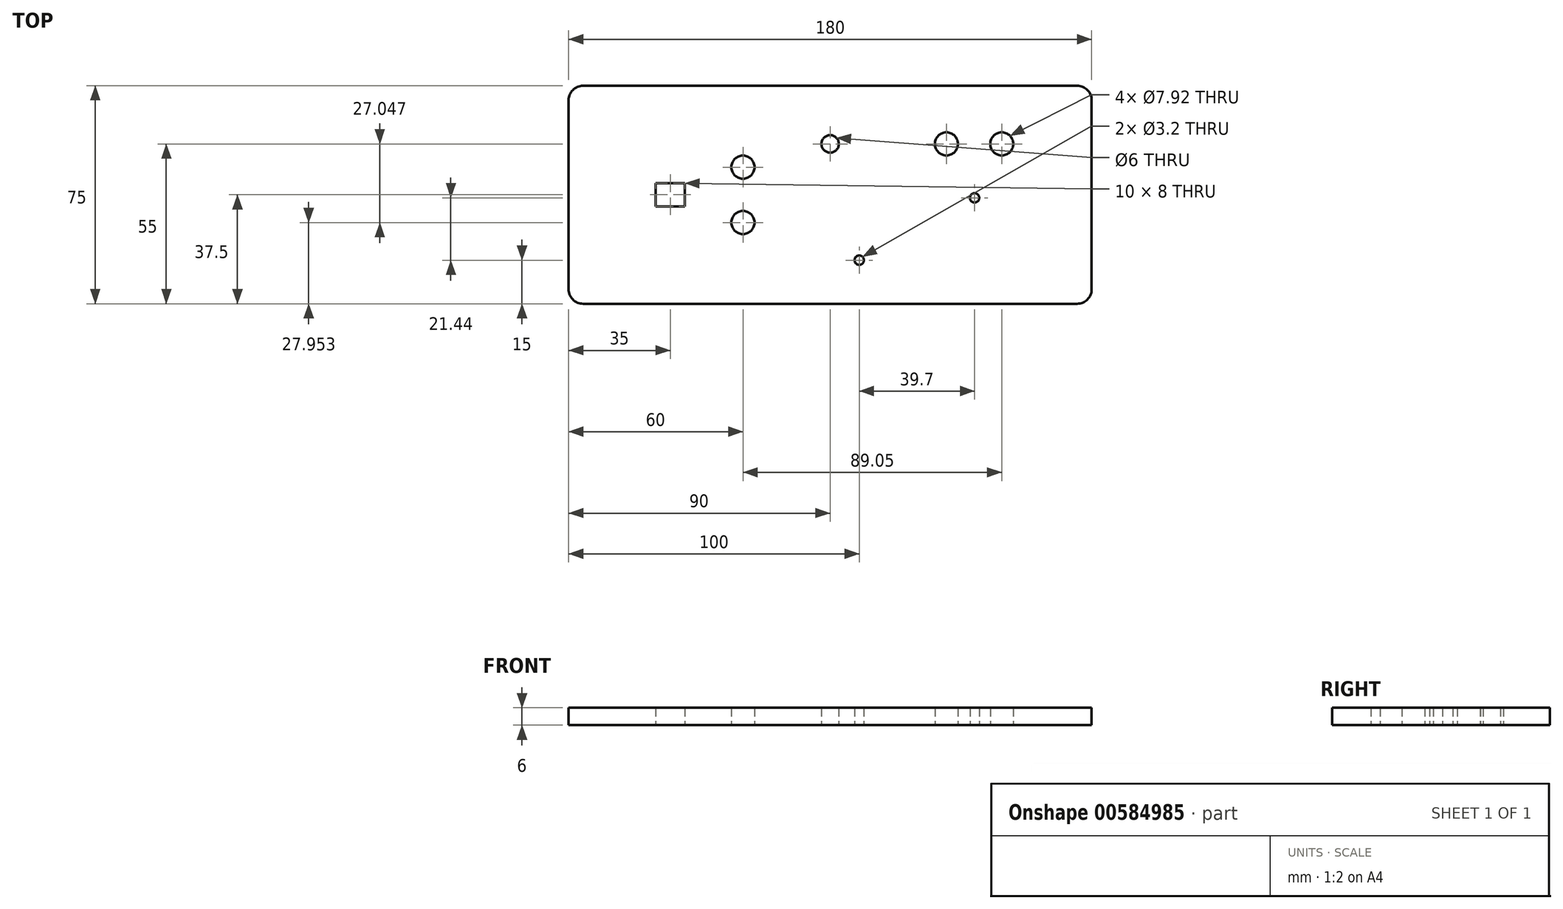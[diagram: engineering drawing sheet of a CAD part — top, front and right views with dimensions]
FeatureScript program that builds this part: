
annotation { "Feature Type Name" : "Feature", "Feature Type Description" : "" }
export const myFeature = defineFeature(function(context is Context, id is Id, definition is map)
    precondition{}
    {
        {
            var Q0;
            Q0=qCreatedBy(makeId("Top.planeOp"),FACE);
            var sketch = newSketch(context, id + "F0", { "sketchPlane" : qUnion([Q0])});
            skLineSegment(sketch, "E0.bottom", {"start": v(-90, 37.5) * mm, "end": v(90, 37.5) * mm});
            skLineSegment(sketch, "E0.top", {"start": v(-90, -37.5) * mm, "end": v(90, -37.5) * mm});
            skLineSegment(sketch, "E0.left", {"start": v(-90, 37.5) * mm, "end": v(-90, -37.5) * mm});
            skLineSegment(sketch, "E0.right", {"start": v(90, 37.5) * mm, "end": v(90, -37.5) * mm});
            skPoint(sketch, "E0.middle", {"position": v(0, 0) * mm});
            skLineSegment(sketch, "E1.bottom", {"start": v(-50, -4) * mm, "end": v(-60, -4) * mm});
            skLineSegment(sketch, "E1.top", {"start": v(-50, 4) * mm, "end": v(-60, 4) * mm});
            skLineSegment(sketch, "E1.left", {"start": v(-50, -4) * mm, "end": v(-50, 4) * mm});
            skLineSegment(sketch, "E1.right", {"start": v(-60, -4) * mm, "end": v(-60, 4) * mm});
            skPoint(sketch, "E1.middle", {"position": v(-55, 0) * mm});
            skCircle(sketch, "E2", {"center": v(-30, 9.5) * mm, "radius": 3.96 * mm});
            skCircle(sketch, "E3", {"center": v(-30, -9.55) * mm, "radius": 3.96 * mm});
            skCircle(sketch, "E4", {"center": v(10, -22.5) * mm, "radius": 1.6 * mm});
            skCircle(sketch, "E5", {"center": v(49.7, -1.06) * mm, "radius": 1.6 * mm});
            skCircle(sketch, "E6", {"center": v(0, 17.5) * mm, "radius": 3 * mm});
            skCircle(sketch, "E7", {"center": v(40, 17.5) * mm, "radius": 3.96 * mm});
            skCircle(sketch, "E8", {"center": v(59.05, 17.5) * mm, "radius": 3.96 * mm});
            skLineSegment(sketch, "E9", {"start": v(-30, 9.5) * mm, "end": v(-30, -9.55) * mm});
            skSolve(sketch);
        }
        {
            var Q0;
            Q0=makeQuery(id+"F0.imprint","IMPRINT",FACE,{"disambiguationData":[TD([[makeQuery(id+"F0.imprint","IMPRINT",EDGE,{"derivedFrom":sQuery(id+"F0.wireOp",EDGE,"E0.bottom")}),-1.0]])]});
            extrude(context, id + "F1", {"entities" : qUnion([Q0]), "depth" : 6 * mm, "offsetDistance" : 25 * mm});
        }
        {
            var Q0;
            Q0=makeQuery(id+"F1.opExtrude","SWEPT_EDGE",EDGE,{"disambiguationData":[OSD([sQuery(id+"F0.wireOp",EDGE,"E0.bottom"),sQuery(id+"F0.wireOp",EDGE,"E0.left")])]});
            var Q1;
            Q1=makeQuery(id+"F1.opExtrude","SWEPT_EDGE",EDGE,{"disambiguationData":[OSD([sQuery(id+"F0.wireOp",EDGE,"E0.bottom"),sQuery(id+"F0.wireOp",EDGE,"E0.right")])]});
            var Q2;
            Q2=makeQuery(id+"F1.opExtrude","SWEPT_EDGE",EDGE,{"disambiguationData":[OSD([sQuery(id+"F0.wireOp",EDGE,"E0.top"),sQuery(id+"F0.wireOp",EDGE,"E0.right")])]});
            var Q3;
            Q3=makeQuery(id+"F1.opExtrude","SWEPT_EDGE",EDGE,{"disambiguationData":[OSD([sQuery(id+"F0.wireOp",EDGE,"E0.top"),sQuery(id+"F0.wireOp",EDGE,"E0.left")])]});
            fillet(context, id + "F2", {"entities" : qUnion([Q0, Q1, Q2, Q3]), "radius" : 5 * mm, "tangentPropagation" : true, "allowEdgeOverflow" : false});
        }
    });
